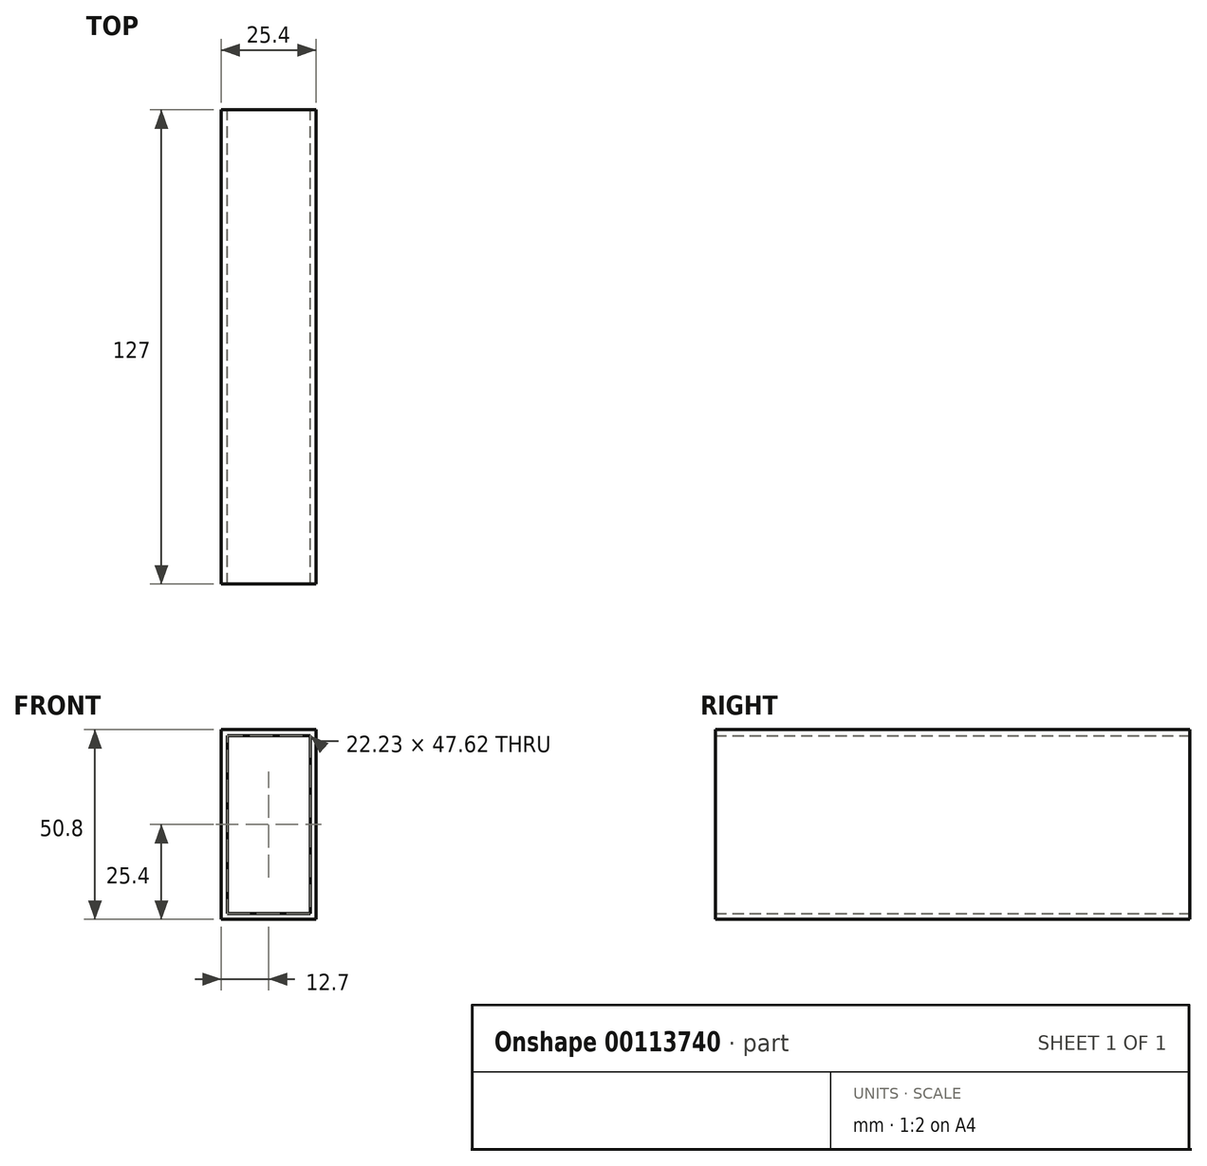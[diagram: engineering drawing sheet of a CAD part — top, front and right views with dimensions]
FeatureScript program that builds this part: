
annotation { "Feature Type Name" : "Feature", "Feature Type Description" : "" }
export const myFeature = defineFeature(function(context is Context, id is Id, definition is map)
    precondition{}
    {
        {
            var Q0;
            Q0=qCreatedBy(makeId("Front.planeOp"),FACE);
            var sketch = newSketch(context, id + "F0", { "sketchPlane" : qUnion([Q0])});
            skLineSegment(sketch, "E0.bottom", {"start": v(25.4, 50.8) * mm, "end": v(0, 50.8) * mm});
            skLineSegment(sketch, "E0.top", {"start": v(25.4, 0) * mm, "end": v(0, 0) * mm});
            skLineSegment(sketch, "E0.left", {"start": v(25.4, 50.8) * mm, "end": v(25.4, 0) * mm});
            skLineSegment(sketch, "E0.right", {"start": v(0, 50.8) * mm, "end": v(0, 0) * mm});
            skPoint(sketch, "E1", {"position": v(1.59, 1.59) * mm});
            skPoint(sketch, "E2", {"position": v(23.81, 49.21) * mm});
            skLineSegment(sketch, "E3.bottom", {"start": v(1.59, 1.59) * mm, "end": v(23.81, 1.59) * mm});
            skLineSegment(sketch, "E3.top", {"start": v(1.59, 49.21) * mm, "end": v(23.81, 49.21) * mm});
            skLineSegment(sketch, "E3.left", {"start": v(1.59, 1.59) * mm, "end": v(1.59, 49.21) * mm});
            skLineSegment(sketch, "E3.right", {"start": v(23.81, 1.59) * mm, "end": v(23.81, 49.21) * mm});
            skSolve(sketch);
        }
        {
            var Q0;
            Q0=makeQuery(id+"F0.imprint","IMPRINT",FACE,{"disambiguationData":[TD([[makeQuery(id+"F0.imprint","IMPRINT",EDGE,{"derivedFrom":sQuery(id+"F0.wireOp",EDGE,"E0.bottom")}),1.0]])]});
            extrude(context, id + "F1", {"entities" : qUnion([Q0]), "depth" : 127 * mm});
        }
    });
